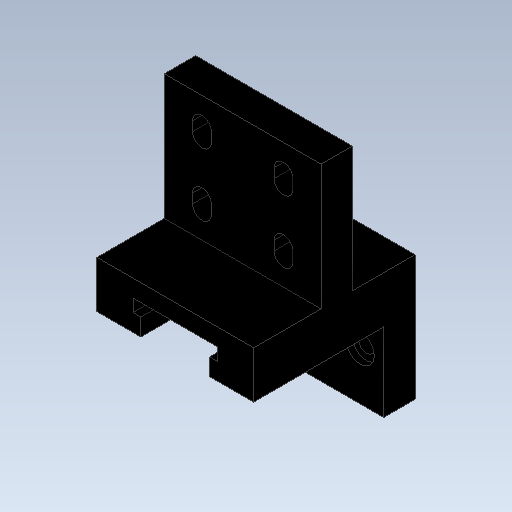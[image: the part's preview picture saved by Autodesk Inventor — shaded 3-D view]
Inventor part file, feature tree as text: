
AUTODESK INVENTOR PART (.ipt)
format: ipt  version: 2020 (Build 240168000, 168)  size: 230,400 bytes
history: native  units: mm
features: sketch x5, extrude x4, plane x1, hole x1, direct_edit x1, move_body x1
ambient origin geometry x8: Origin, YZ Plane, XZ Plane, XY Plane, X Axis, Y Axis, Z Axis, Center Point
bodies: Solid1 (feature_tree)
feature tree (13):
  extrude  "Extrusion1"  Depth=10.0mm
  plane  "Work Plane1"
  extrude  "Extrusion16"  Depth=50.0mm TaperAngle=0.0deg
  extrude  "Extrusion17"  Depth=25.0mm
  hole  "Hole5"  [1 undecoded]
  direct_edit  "Direct Edit6"
  extrude  "Extrusion18"  Depth=4.0mm
  sketch  "Sketch1"  dims[d0=55.0mm d1=10.0mm]
  sketch  "Sketch23"  dims[d3=51.5mm d4=50.0mm d5=0.0mm]
  sketch  "Sketch24"  dims[d27=-32.75mm d135=25.0mm]
  sketch  "Sketch25"  dims[d144=20.0mm d145=40.0mm]
  sketch  "Sketch26"  dims[d149=9.5mm d150=4.0mm d151=2.5mm d152=27.0mm d153=10.0mm d154=0.0mm d155=10.0mm d156=5.0mm d157=0.0mm d158=0.0mm d162=5.0mm d163=15.5mm d164=7.5mm d165=35.0mm d166=5.0mm d167=6.0mm d168=9.0mm d169=2.0mm d170=90.0deg d171=8.0mm d172=20.594885mm d173=3.0mm d174=6.0mm d175=10.0mm d176=12.0mm d177=12.0mm d178=10.0mm d179=0.0mm d180=0.0mm d181=0.0mm d182=0.0mm d183=-5.0mm d185=10.0mm]
  move_body  "Move6"
note: 1 required parameter value undecoded (feature->parameter linkage not recoverable at this tier; creation-order binding heuristic only, values carry confidence <= 0.55)
